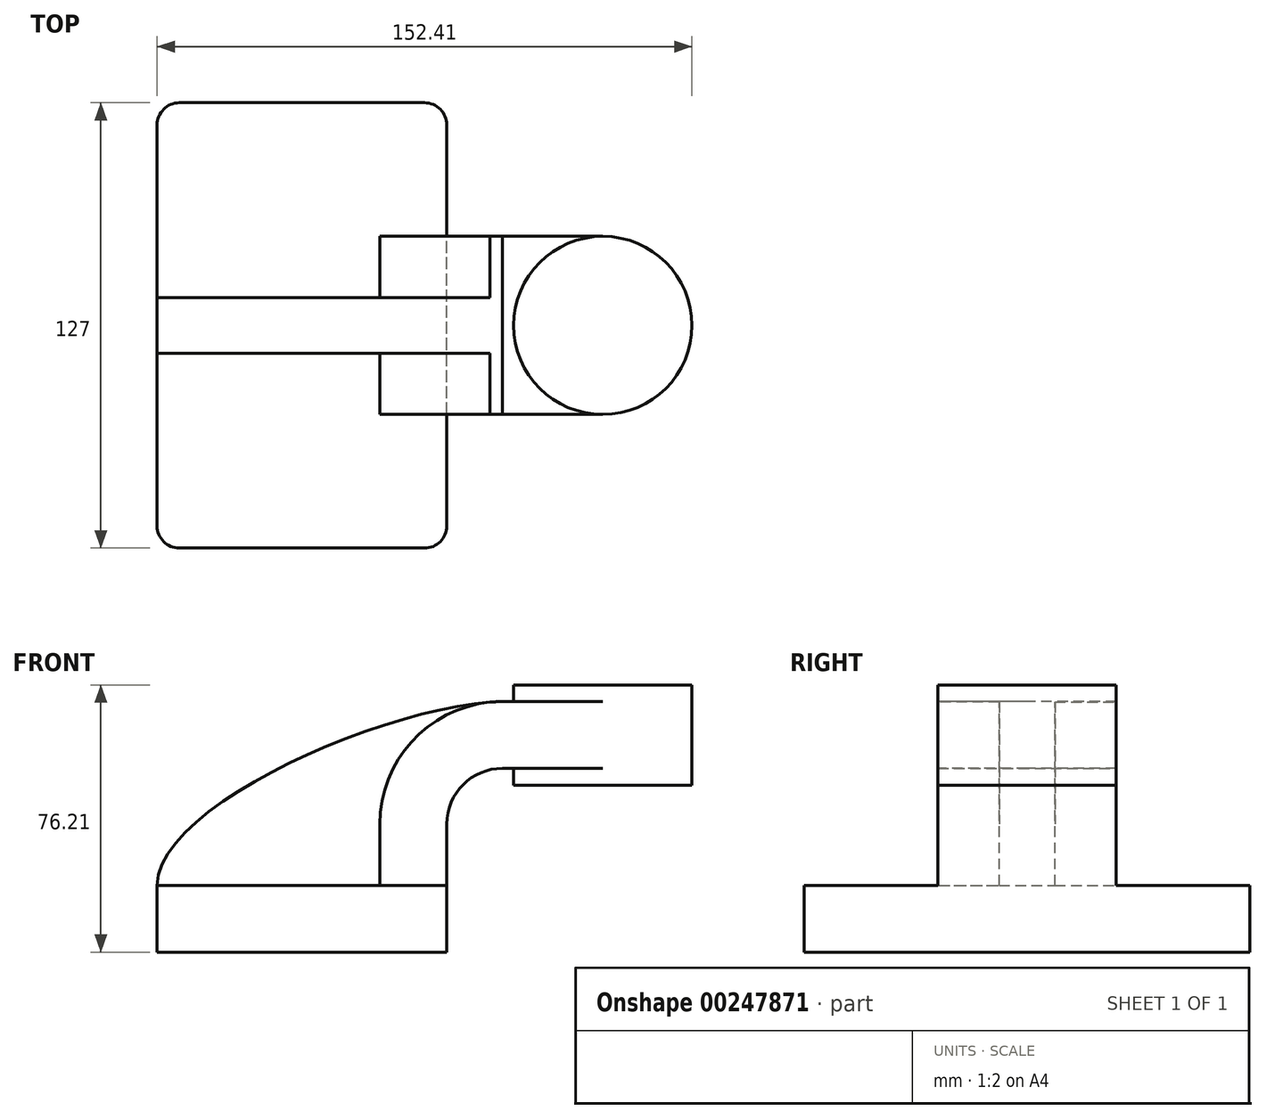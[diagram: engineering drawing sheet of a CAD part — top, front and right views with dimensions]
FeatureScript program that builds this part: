
annotation { "Feature Type Name" : "Feature", "Feature Type Description" : "" }
export const myFeature = defineFeature(function(context is Context, id is Id, definition is map)
    precondition{}
    {
        {
            var Q0;
            Q0=qCreatedBy(makeId("Front.planeOp"),FACE);
            var sketch = newSketch(context, id + "F0", { "sketchPlane" : qUnion([Q0])});
            skLineSegment(sketch, "E0.bottom", {"start": v(-41.28, -9.53) * mm, "end": v(41.28, -9.53) * mm});
            skLineSegment(sketch, "E0.top", {"start": v(-41.28, 9.52) * mm, "end": v(41.28, 9.52) * mm});
            skLineSegment(sketch, "E0.left", {"start": v(-41.28, -9.53) * mm, "end": v(-41.28, 9.52) * mm});
            skLineSegment(sketch, "E0.right", {"start": v(41.28, -9.53) * mm, "end": v(41.28, 9.52) * mm});
            skPoint(sketch, "E0.middle", {"position": v(0, 0) * mm});
            skLineSegment(sketch, "E1.bottom", {"start": v(60.33, 38.1) * mm, "end": v(111.13, 38.1) * mm});
            skLineSegment(sketch, "E1.top", {"start": v(60.33, 66.68) * mm, "end": v(111.13, 66.68) * mm});
            skLineSegment(sketch, "E1.left", {"start": v(60.33, 38.1) * mm, "end": v(60.33, 66.68) * mm});
            skLineSegment(sketch, "E1.right", {"start": v(111.13, 38.1) * mm, "end": v(111.13, 66.68) * mm});
            skPoint(sketch, "E1.middle", {"position": v(85.73, 52.39) * mm});
            skLineSegment(sketch, "E2", {"start": v(41.27, 9.52) * mm, "end": v(41.27, 27) * mm});
            skArc(sketch, "E3", {"start": v(41.28, 27) * mm, "mid": v(45.92, 38.23) * mm, "end": v(57.15, 42.88) * mm});
            skLineSegment(sketch, "E4", {"start": v(57.15, 42.88) * mm, "end": v(85.73, 42.88) * mm});
            skLineSegment(sketch, "E5.0", {"start": v(57.15, 61.93) * mm, "end": v(85.73, 61.93) * mm});
            skArc(sketch, "E5.1", {"start": v(22.23, 27) * mm, "mid": v(32.45, 51.7) * mm, "end": v(57.15, 61.93) * mm});
            skLineSegment(sketch, "E5.2", {"start": v(22.23, 9.52) * mm, "end": v(22.23, 27) * mm});
            skLineSegment(sketch, "E6", {"start": v(85.73, 38.1) * mm, "end": v(85.73, 66.68) * mm});
            skFitSpline(sketch, "E7", {"points": [v(-41.28, 9.53) * mm, v(57.15, 61.93) * mm], "startDerivative": vector(1.1, 69.88) * mm, "endDerivative": vector(96.23, 2.19) * mm});
            skSolve(sketch);
        }
        {
            var Q0;
            Q0=makeQuery(id+"F0.imprint","IMPRINT",FACE,{"disambiguationData":[TD([[makeQuery(id+"F0.imprint","IMPRINT",EDGE,{"derivedFrom":sQuery(id+"F0.wireOp",EDGE,"E0.bottom")}),1.0]])]});
            extrude(context, id + "F1", {"entities" : qUnion([Q0]), "endBound" : BoundingType.SYMMETRIC, "depth" : 127 * mm});
        }
        {
            var Q0;
            {var subQ1=sQuery(id+"F0.wireOp",EDGE,"E2");Q0=makeQuery(id+"F0.imprint","IMPRINT",FACE,{"disambiguationData":[TD([[makeQuery(id+"F0.imprint","IMPRINT",EDGE,{"derivedFrom":subQ1}),1.0]])]});}
            extrude(context, id + "F2", {"entities" : qUnion([Q0]), "operationType" : NewBodyOperationType.ADD, "endBound" : BoundingType.SYMMETRIC, "depth" : 50.8 * mm});
        }
        {
            var Q0;
            {var subQ0=sQuery(id+"F0.wireOp",EDGE,"E4");var subQ1=sQuery(id+"F0.wireOp",EDGE,"E1.left");var subQ2=makeQuery(id+"F0.imprint","INTERSECT",VERTEX,{"derivedFrom":[subQ1,subQ0]});Q0=makeQuery(id+"F0.imprint","IMPRINT",FACE,{"disambiguationData":[TD([[makeQuery(id+"F0.imprint","IMPRINT",EDGE,{"disambiguationData":[TD([[subQ2,-1.0]])],"derivedFrom":subQ1}),-1.0]])]});}
            extrude(context, id + "F3", {"entities" : qUnion([Q0]), "operationType" : NewBodyOperationType.ADD, "endBound" : BoundingType.SYMMETRIC, "depth" : 50.8 * mm});
        }
        {
            var Q0;
            {var subQ3=sQuery(id+"F0.wireOp",EDGE,"E5.2");Q0=makeQuery(id+"F0.imprint","IMPRINT",FACE,{"disambiguationData":[TD([[makeQuery(id+"F0.imprint","IMPRINT",EDGE,{"derivedFrom":subQ3}),1.0]])]});}
            extrude(context, id + "F4", {"entities" : qUnion([Q0]), "operationType" : NewBodyOperationType.ADD, "endBound" : BoundingType.SYMMETRIC, "depth" : 15.88 * mm});
        }
        {
            var Q0;
            {var subQ0=sQuery(id+"F0.wireOp",EDGE,"E1.right");Q0=makeQuery(id+"F0.imprint","IMPRINT",FACE,{"disambiguationData":[TD([[makeQuery(id+"F0.imprint","IMPRINT",EDGE,{"derivedFrom":subQ0}),1.0]])]});}
            var Q1;
            Q1=sQuery(id+"F0.wireOp",EDGE,"E6");
            revolve(context, id + "F5", {"operationType" : NewBodyOperationType.ADD, "entities" : qUnion([Q0]), "axis" : qUnion([Q1]), "revolveType" : RevolveType.FULL});
        }
        {
            var Q0;
            Q0=makeQuery(id+"F1.opExtrude","CAP_EDGE",EDGE,{"disambiguationData":[OSD([sQuery(id+"F0.wireOp",EDGE,"E0.left")])],"isStart":false});
            var Q1;
            Q1=makeQuery(id+"F1.opExtrude","CAP_EDGE",EDGE,{"disambiguationData":[OSD([sQuery(id+"F0.wireOp",EDGE,"E0.right")])],"isStart":false});
            var Q2;
            Q2=makeQuery(id+"F1.opExtrude","CAP_EDGE",EDGE,{"disambiguationData":[OSD([sQuery(id+"F0.wireOp",EDGE,"E0.left")])],"isStart":true});
            var Q3;
            Q3=makeQuery(id+"F1.opExtrude","CAP_EDGE",EDGE,{"disambiguationData":[OSD([sQuery(id+"F0.wireOp",EDGE,"E0.right")])],"isStart":true});
            fillet(context, id + "F6", {"entities" : qUnion([Q0, Q1, Q2, Q3]), "radius" : 6.35 * mm, "tangentPropagation" : true, "allowEdgeOverflow" : false});
        }
    });
